# Revit family: Arrow Screen
name_source: partatom
category: Furniture
units: mm (PartAtom-declared; Revit-internal decimal feet)

## family parameters
Always vertical = Yes
Cut with Voids When Loaded = No
OmniClass Number = 23.40.20.00
OmniClass Title = General Furniture and Specialties
Room Calculation Point = No
Shared = No
Work Plane-Based = No

## types (7) — shared parameters
Assembly Code = E2020200
Manufacturer = Gresham Office Furniture
Model = MIRAGE LITE
Product Data Specification = https://gof.co.uk
Range = SCREENS
Screen = GABRIEL Byron_14101
URL = www.gof.co.uk

## per-type parameters (varying)
| type | Product Code | Width |
| 1970 x 380 High Screen | ML2004-6 | 1970 mm  [stored 6.46325 ft] |
| 1770 x 380 High Screen | ML1804-6 | 1770 mm |
| 1570 x 380 High Screen | ML1604-6 | 1570 mm |
| 1370 x 380 High Screen | ML1404-6 | 1370 mm |
| 1170 x 380 High Screen | ML1204-6 | 1170 mm  [stored 3.83858 ft] |
| 970 x 380 High Screen | ML1004-6 | 970 mm  [stored 3.18241 ft] |
| 770 x 380 High Screen | ML0804-6 | 770 mm  [stored 2.52625 ft] |

note: [stored X ft] marks values corroborated as IEEE doubles in the binary element streams (Revit-internal decimal feet)

## geometry (parser evidence)
native form markers: Sweep x3
no freeform markers — native parametric forms only
